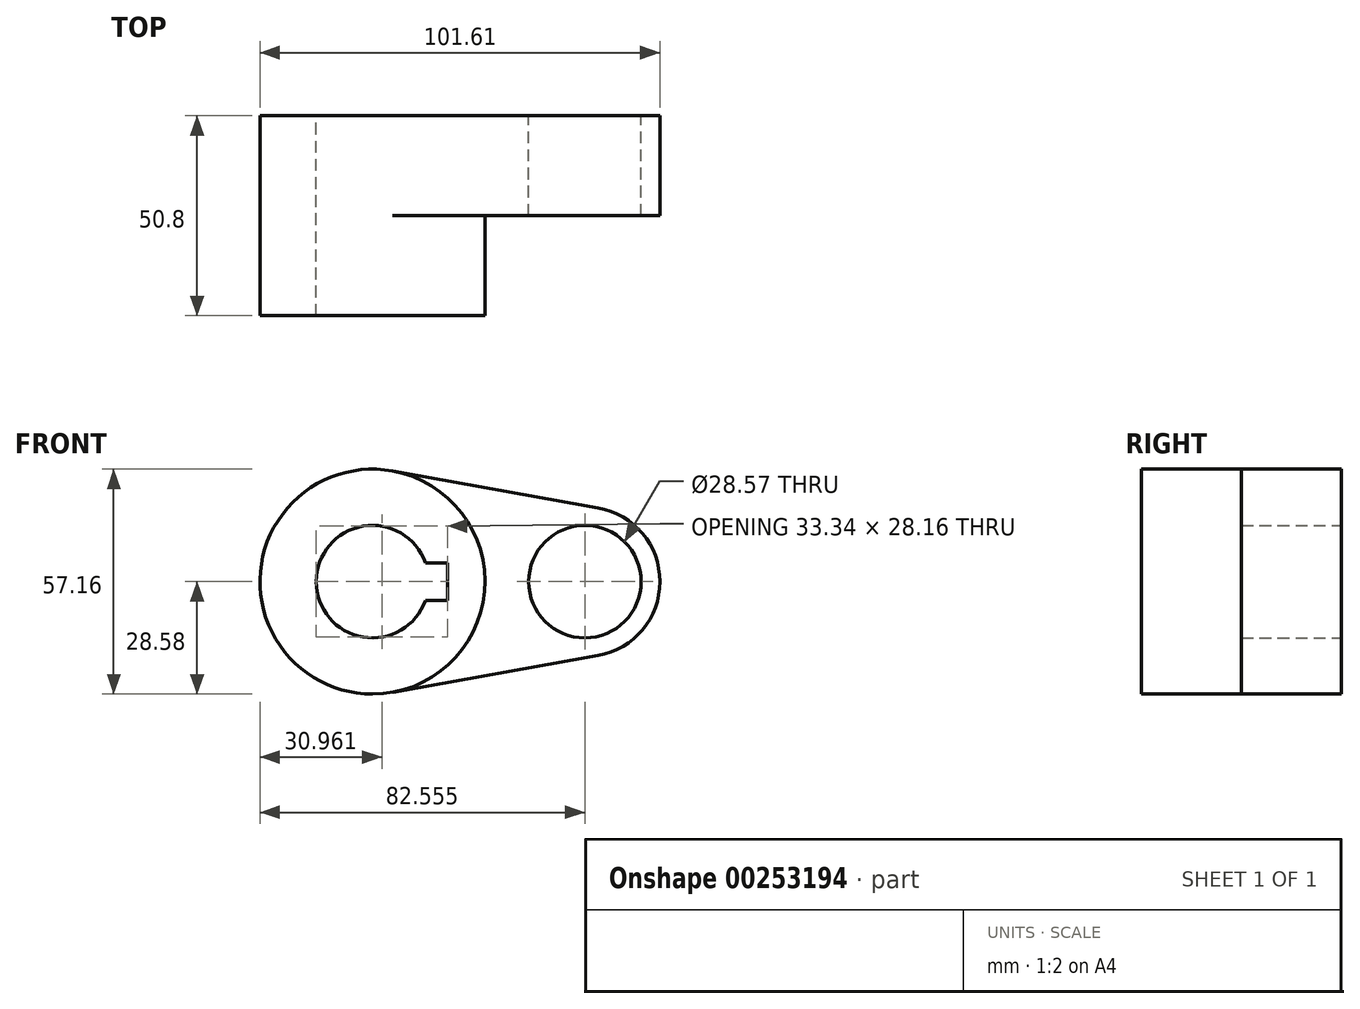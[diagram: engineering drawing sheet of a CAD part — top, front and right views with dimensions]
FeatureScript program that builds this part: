
annotation { "Feature Type Name" : "Feature", "Feature Type Description" : "" }
export const myFeature = defineFeature(function(context is Context, id is Id, definition is map)
    precondition{}
    {
        {
            var Q0;
            Q0=qCreatedBy(makeId("Front.planeOp"),FACE);
            var sketch = newSketch(context, id + "F0", { "sketchPlane" : qUnion([Q0])});
            skCircle(sketch, "E0", {"center": v(0, 0) * mm, "radius": 28.58 * mm});
            skCircle(sketch, "E1", {"center": v(53.98, 0) * mm, "radius": 19.05 * mm});
            skCircle(sketch, "E2", {"center": v(0, 0) * mm, "radius": 14.29 * mm});
            skCircle(sketch, "E3", {"center": v(53.98, 0) * mm, "radius": 14.29 * mm});
            skLineSegment(sketch, "E4.bottom", {"start": v(19.05, -4.76) * mm, "end": v(-19.05, -4.76) * mm});
            skLineSegment(sketch, "E4.top", {"start": v(19.05, 4.76) * mm, "end": v(-19.05, 4.76) * mm});
            skLineSegment(sketch, "E4.left", {"start": v(19.05, -4.76) * mm, "end": v(19.05, 4.76) * mm});
            skLineSegment(sketch, "E4.right", {"start": v(-19.05, -4.76) * mm, "end": v(-19.05, 4.76) * mm});
            skLineSegment(sketch, "E5", {"start": v(5.04, 28.13) * mm, "end": v(57.34, 18.75) * mm});
            skLineSegment(sketch, "E6", {"start": v(5.04, -28.13) * mm, "end": v(57.34, -18.75) * mm});
            skSolve(sketch);
        }
        {
            var Q0;
            Q0 = qSketchRegion(id + "F0", true);
            extrude(context, id + "F1", {"entities" : qUnion([Q0]), "depth" : 25.4 * mm});
        }
        {
            var Q0;
            {var subQ4=sQuery(id+"F0.wireOp",EDGE,"E4.left");Q0=makeQuery(id+"F0.imprint","IMPRINT",FACE,{"disambiguationData":[TD([[makeQuery(id+"F0.imprint","IMPRINT",EDGE,{"derivedFrom":subQ4}),-1.0]])]});}
            var Q1;
            {var subQ5=sQuery(id+"F0.wireOp",EDGE,"E4.right");Q1=makeQuery(id+"F0.imprint","IMPRINT",FACE,{"disambiguationData":[TD([[makeQuery(id+"F0.imprint","IMPRINT",EDGE,{"derivedFrom":subQ5}),-1.0]])]});}
            extrude(context, id + "F2", {"entities" : qUnion([Q0, Q1]), "operationType" : NewBodyOperationType.ADD, "depth" : 50.8 * mm});
        }
    });
